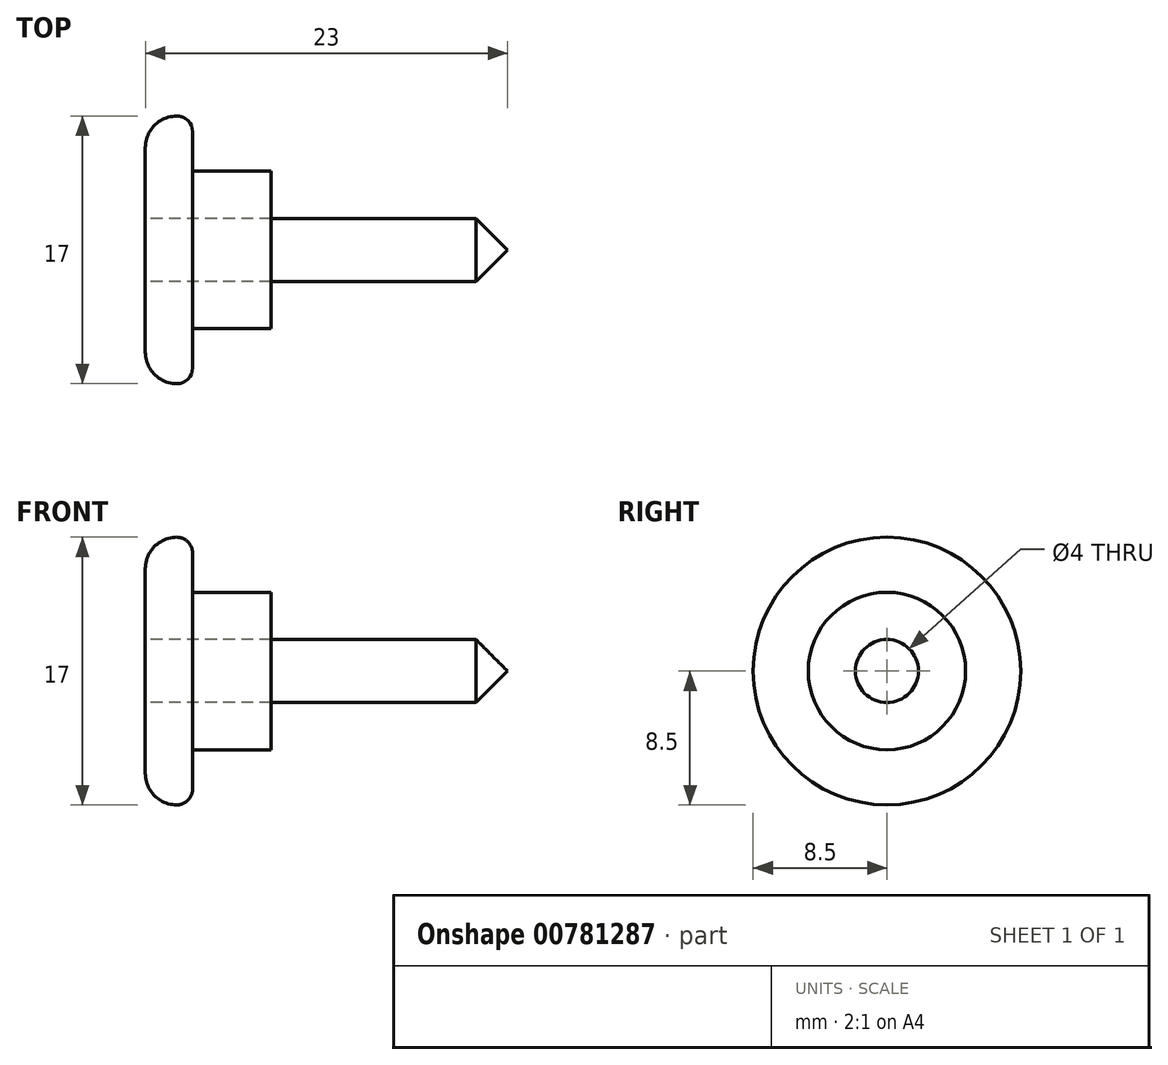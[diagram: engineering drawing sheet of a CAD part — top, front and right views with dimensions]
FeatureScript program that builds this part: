
annotation { "Feature Type Name" : "Feature", "Feature Type Description" : "" }
export const myFeature = defineFeature(function(context is Context, id is Id, definition is map)
    precondition{}
    {
        {
            var Q0;
            Q0=qCreatedBy(makeId("Front.planeOp"),FACE);
            var sketch = newSketch(context, id + "F0", { "sketchPlane" : qUnion([Q0])});
            skLineSegment(sketch, "E0.bottom", {"start": v(-17.7, 8.5) * mm, "end": v(-20.7, 8.5) * mm});
            skLineSegment(sketch, "E0.top", {"start": v(-17.7, -8.5) * mm, "end": v(-20.7, -8.5) * mm});
            skLineSegment(sketch, "E0.left", {"start": v(-17.7, 8.5) * mm, "end": v(-17.7, -8.5) * mm});
            skLineSegment(sketch, "E0.right", {"start": v(-20.7, 8.5) * mm, "end": v(-20.7, -8.5) * mm});
            skPoint(sketch, "E0.middle", {"position": v(-19.2, 0) * mm});
            skLineSegment(sketch, "E1.bottom", {"start": v(-17.7, 5) * mm, "end": v(-12.7, 5) * mm});
            skLineSegment(sketch, "E1.top", {"start": v(-17.7, -5) * mm, "end": v(-12.7, -5) * mm});
            skLineSegment(sketch, "E1.left", {"start": v(-17.7, 5) * mm, "end": v(-17.7, -5) * mm});
            skLineSegment(sketch, "E1.right", {"start": v(-12.7, 5) * mm, "end": v(-12.7, -5) * mm});
            skPoint(sketch, "E1.middle", {"position": v(-15.2, 0) * mm});
            skPoint(sketch, "E2.middle", {"position": v(-11.7, 0) * mm});
            skLineSegment(sketch, "E3.left", {"start": v(-12.7, 2) * mm, "end": v(-12.7, -2) * mm});
            skLineSegment(sketch, "E3.right", {"start": v(2.3, 2) * mm, "end": v(2.3, -2) * mm});
            skPoint(sketch, "E3.middle", {"position": v(-5.2, 0) * mm});
            skLineSegment(sketch, "E4", {"start": v(-20.7, 0) * mm, "end": v(2.3, 0) * mm});
            skLineSegment(sketch, "E5.bottom", {"start": v(2.3, 2) * mm, "end": v(-20.7, 2) * mm});
            skLineSegment(sketch, "E5.top", {"start": v(2.3, -2) * mm, "end": v(-20.7, -2) * mm});
            skLineSegment(sketch, "E5.right", {"start": v(-20.7, 2) * mm, "end": v(-20.7, -2) * mm});
            skSolve(sketch);
        }
        {
            var Q0;
            {var subQ6=sQuery(id+"F0.wireOp",EDGE,"E0.bottom");Q0=makeQuery(id+"F0.imprint","IMPRINT",FACE,{"disambiguationData":[TD([[makeQuery(id+"F0.imprint","IMPRINT",EDGE,{"derivedFrom":subQ6}),1.0]])]});}
            var Q1;
            {var subQ0=sQuery(id+"F0.wireOp",EDGE,"E1.bottom");Q1=makeQuery(id+"F0.imprint","IMPRINT",FACE,{"disambiguationData":[TD([[makeQuery(id+"F0.imprint","IMPRINT",EDGE,{"derivedFrom":subQ0}),-1.0]])]});}
            var Q2;
            {var subQ1=sQuery(id+"F0.wireOp",EDGE,"E2.bottom");Q2=makeQuery(id+"F0.imprint","IMPRINT",FACE,{"disambiguationData":[TD([[makeQuery(id+"F0.imprint","IMPRINT",EDGE,{"derivedFrom":subQ1}),-1.0]])]});}
            var Q3;
            {var subQ0=sQuery(id+"F0.wireOp",EDGE,"E3.bottom");Q3=makeQuery(id+"F0.imprint","IMPRINT",FACE,{"disambiguationData":[TD([[makeQuery(id+"F0.imprint","IMPRINT",EDGE,{"derivedFrom":subQ0}),-1.0]])]});}
            var Q4;
            {var subQ3=sQuery(id+"F0.wireOp",EDGE,"E4");var subQ5=sQuery(id+"F0.wireOp",EDGE,"E3.right");var subQ7=makeQuery(id+"F0.imprint","INTERSECT",VERTEX,{"derivedFrom":[subQ3,subQ5]});Q4=makeQuery(id+"F0.imprint","IMPRINT",FACE,{"disambiguationData":[TD([[makeQuery(id+"F0.imprint","IMPRINT",EDGE,{"disambiguationData":[TD([[subQ7,1.0]])],"derivedFrom":subQ3}),1.0]])]});}
            var Q5;
            {var subQ0=sQuery(id+"F0.wireOp",EDGE,"E4");var subQ1=sQuery(id+"F0.wireOp",EDGE,"E1.left");var subQ2=makeQuery(id+"F0.imprint","INTERSECT",VERTEX,{"derivedFrom":[subQ1,subQ0]});Q5=makeQuery(id+"F0.imprint","IMPRINT",FACE,{"disambiguationData":[TD([[makeQuery(id+"F0.imprint","IMPRINT",EDGE,{"disambiguationData":[TD([[subQ2,-1.0]])],"derivedFrom":subQ1}),1.0]])]});}
            var Q6;
            {var subQ0=sQuery(id+"F0.wireOp",EDGE,"E4");var subQ1=sQuery(id+"F0.wireOp",EDGE,"E1.left");var subQ2=makeQuery(id+"F0.imprint","INTERSECT",VERTEX,{"derivedFrom":[subQ1,subQ0]});Q6=makeQuery(id+"F0.imprint","IMPRINT",FACE,{"disambiguationData":[TD([[makeQuery(id+"F0.imprint","IMPRINT",EDGE,{"disambiguationData":[TD([[subQ2,-1.0]])],"derivedFrom":subQ1}),-1.0]])]});}
            var Q7;
            Q7=sQuery(id+"F0.wireOp",EDGE,"E4");
            revolve(context, id + "F1", {"surfaceOperationType" : NewSurfaceOperationType.NEW, "entities" : qUnion([Q0, Q1, Q2, Q3, Q4, Q5, Q6]), "axis" : qUnion([Q7]), "revolveType" : RevolveType.FULL});
        }
        {
            var Q0;
            Q0=makeQuery(id+"F1.opRevolve","SWEPT_EDGE",EDGE,{"disambiguationData":[OSD([sQuery(id+"F0.wireOp",EDGE,"E5.bottom"),sQuery(id+"F0.wireOp",EDGE,"E3.right")])]});
            chamfer(context, id + "F2", {"entities" : qUnion([Q0]), "width" : 2 * mm, "tangentPropagation" : true});
        }
        {
            var Q0;
            Q0=makeQuery(id+"F1.opRevolve","SWEPT_EDGE",EDGE,{"disambiguationData":[OSD([sQuery(id+"F0.wireOp",EDGE,"E0.bottom"),sQuery(id+"F0.wireOp",EDGE,"E0.right")])]});
            fillet(context, id + "F3", {"entities" : qUnion([Q0]), "radius" : 2 * mm, "tangentPropagation" : true, "allowEdgeOverflow" : false});
        }
        {
            var Q0;
            Q0=makeQuery(id+"F1.opRevolve","SWEPT_EDGE",EDGE,{"disambiguationData":[OSD([sQuery(id+"F0.wireOp",EDGE,"E2.bottom"),sQuery(id+"F0.wireOp",EDGE,"E2.left")])]});
            var Q1;
            Q1=makeQuery(id+"F1.opRevolve","SWEPT_EDGE",EDGE,{"disambiguationData":[OSD([sQuery(id+"F0.wireOp",EDGE,"E0.bottom"),sQuery(id+"F0.wireOp",EDGE,"E0.left")])]});
            fillet(context, id + "F4", {"entities" : qUnion([Q0, Q1]), "radius" : 1 * mm, "tangentPropagation" : true, "allowEdgeOverflow" : false});
        }
    });
